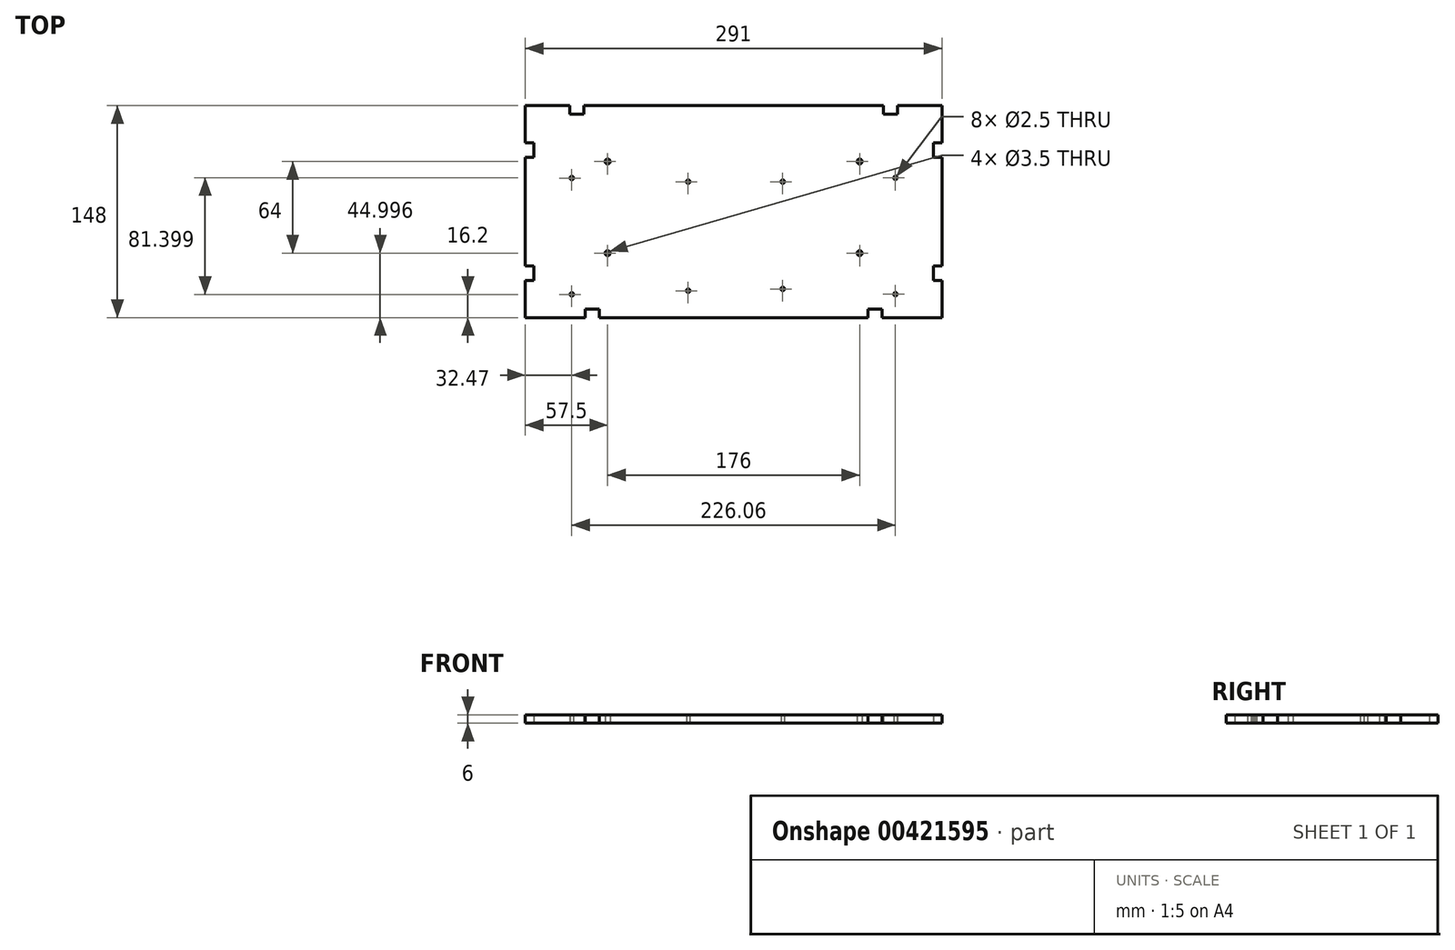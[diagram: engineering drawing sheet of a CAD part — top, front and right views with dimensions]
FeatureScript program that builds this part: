
annotation { "Feature Type Name" : "Feature", "Feature Type Description" : "" }
export const myFeature = defineFeature(function(context is Context, id is Id, definition is map)
    precondition{}
    {
        {
            var Q0;
            Q0=qCreatedBy(makeId("Top.planeOp"),FACE);
            var sketch = newSketch(context, id + "F0", { "sketchPlane" : qUnion([Q0])});
            skLineSegment(sketch, "E0", {"start": v(145.5, 47.8) * mm, "end": v(145.5, -28.2) * mm});
            skLineSegment(sketch, "E1", {"start": v(114.5, 83.8) * mm, "end": v(114.5, 77.8) * mm});
            skLineSegment(sketch, "E2", {"start": v(145.5, 83.8) * mm, "end": v(145.5, 57.8) * mm});
            skLineSegment(sketch, "E3", {"start": v(139.5, -38.2) * mm, "end": v(145.5, -38.2) * mm});
            skLineSegment(sketch, "E4", {"start": v(145.5, 57.8) * mm, "end": v(139.5, 57.8) * mm});
            skLineSegment(sketch, "E5", {"start": v(145.5, 47.8) * mm, "end": v(139.5, 47.8) * mm});
            skLineSegment(sketch, "E6", {"start": v(114.5, 83.8) * mm, "end": v(145.5, 83.8) * mm});
            skLineSegment(sketch, "E7", {"start": v(145.5, -38.2) * mm, "end": v(145.5, -64.2) * mm});
            skLineSegment(sketch, "E8", {"start": v(104.5, 83.8) * mm, "end": v(0, 83.8) * mm});
            skLineSegment(sketch, "E9.MirrorCS", {"start": v(-139.5, -38.2) * mm, "end": v(-145.5, -38.2) * mm});
            skLineSegment(sketch, "E10.MirrorCS", {"start": v(-114.5, 83.8) * mm, "end": v(-114.5, 77.8) * mm});
            skLineSegment(sketch, "E11.MirrorCS", {"start": v(-145.5, 83.8) * mm, "end": v(-145.5, 57.8) * mm});
            skLineSegment(sketch, "E12.MirrorCS", {"start": v(-145.5, -64.2) * mm, "end": v(-103.71, -64.2) * mm});
            skLineSegment(sketch, "E13.MirrorCS", {"start": v(-104.5, 83.8) * mm, "end": v(0, 83.8) * mm});
            skLineSegment(sketch, "E14.MirrorCS", {"start": v(-145.5, -38.2) * mm, "end": v(-145.5, -64.2) * mm});
            skLineSegment(sketch, "E15.MirrorCS", {"start": v(-93.67, -64.2) * mm, "end": v(0, -64.2) * mm});
            skLineSegment(sketch, "E16.MirrorCS", {"start": v(-114.5, 83.8) * mm, "end": v(-145.5, 83.8) * mm});
            skLineSegment(sketch, "E17.MirrorCS", {"start": v(-145.5, 47.8) * mm, "end": v(-145.5, -28.2) * mm});
            skCircle(sketch, "E18", {"center": v(-113.03, 33.28) * mm, "radius": 1.25 * mm});
            skCircle(sketch, "E19", {"center": v(-31.75, 30.74) * mm, "radius": 1.25 * mm});
            skCircle(sketch, "E20.MirrorC", {"center": v(113.03, 33.4) * mm, "radius": 1.25 * mm});
            skCircle(sketch, "E21.MirrorC", {"center": v(34.29, 30.74) * mm, "radius": 1.25 * mm});
            skCircle(sketch, "E22.MirrorC", {"center": v(113.03, -47.88) * mm, "radius": 1.25 * mm});
            skCircle(sketch, "E23.MirrorC", {"center": v(-31.75, -45.46) * mm, "radius": 1.25 * mm});
            skCircle(sketch, "E24.MirrorC", {"center": v(-113.03, -48) * mm, "radius": 1.25 * mm});
            skCircle(sketch, "E25", {"center": v(34.3, -44.2) * mm, "radius": 1.25 * mm});
            skLineSegment(sketch, "E26", {"start": v(103.71, -64.2) * mm, "end": v(145.5, -64.2) * mm});
            skLineSegment(sketch, "E27", {"start": v(0, -64.2) * mm, "end": v(93.67, -64.2) * mm});
            skCircle(sketch, "E28", {"center": v(-88, -19.2) * mm, "radius": 1.75 * mm});
            skCircle(sketch, "E29.MirrorC", {"center": v(88, -19.2) * mm, "radius": 1.75 * mm});
            skCircle(sketch, "E30", {"center": v(-88, 44.8) * mm, "radius": 1.75 * mm});
            skCircle(sketch, "E31.MirrorC", {"center": v(88, 44.8) * mm, "radius": 1.75 * mm});
            skLineSegment(sketch, "E32", {"start": v(114.5, 77.8) * mm, "end": v(104.5, 77.8) * mm});
            skLineSegment(sketch, "E33", {"start": v(104.5, 77.8) * mm, "end": v(104.5, 83.8) * mm});
            skLineSegment(sketch, "E34", {"start": v(139.5, 57.8) * mm, "end": v(139.5, 47.8) * mm});
            skLineSegment(sketch, "E35", {"start": v(139.5, -38.2) * mm, "end": v(139.5, -28.2) * mm});
            skLineSegment(sketch, "E36", {"start": v(139.5, -28.2) * mm, "end": v(145.5, -28.2) * mm});
            skLineSegment(sketch, "E37", {"start": v(103.71, -64.2) * mm, "end": v(103.71, -58.2) * mm});
            skLineSegment(sketch, "E38", {"start": v(103.71, -58.2) * mm, "end": v(93.67, -58.2) * mm});
            skLineSegment(sketch, "E39", {"start": v(93.67, -58.2) * mm, "end": v(93.67, -64.2) * mm});
            skLineSegment(sketch, "E40.MirrorCS", {"start": v(-103.71, -58.2) * mm, "end": v(-93.67, -58.2) * mm});
            skLineSegment(sketch, "E41.MirrorCS", {"start": v(-93.67, -58.2) * mm, "end": v(-93.67, -64.2) * mm});
            skLineSegment(sketch, "E42.MirrorCS", {"start": v(-103.71, -64.2) * mm, "end": v(-103.71, -58.2) * mm});
            skLineSegment(sketch, "E43.MirrorCS", {"start": v(-139.5, -38.2) * mm, "end": v(-139.5, -28.2) * mm});
            skLineSegment(sketch, "E44.MirrorCS", {"start": v(-139.5, -28.2) * mm, "end": v(-145.5, -28.2) * mm});
            skLineSegment(sketch, "E45.MirrorCS", {"start": v(-139.5, 57.8) * mm, "end": v(-139.5, 47.8) * mm});
            skLineSegment(sketch, "E46.MirrorCS", {"start": v(-145.5, 57.8) * mm, "end": v(-139.5, 57.8) * mm});
            skLineSegment(sketch, "E47.MirrorCS", {"start": v(-145.5, 47.8) * mm, "end": v(-139.5, 47.8) * mm});
            skLineSegment(sketch, "E48.MirrorCS", {"start": v(-114.5, 77.8) * mm, "end": v(-104.5, 77.8) * mm});
            skLineSegment(sketch, "E49.MirrorCS", {"start": v(-104.5, 77.8) * mm, "end": v(-104.5, 83.8) * mm});
            skSolve(sketch);
        }
        {
            var Q0;
            {var subQ2=sQuery(id+"F0.wireOp",EDGE,"XMeffzy6-l1vr-bFuy-l6tU-98MnWEfm23K2.bottom");Q0=makeQuery(id+"F0.imprint","IMPRINT",FACE,{"disambiguationData":[TD([[makeQuery(id+"F0.imprint","IMPRINT",EDGE,{"derivedFrom":subQ2}),1.0]])]});}
            var Q1;
            {var subQ0=sQuery(id+"F0.wireOp",EDGE,"LvRFwu82-oml2-OgSb-w6ea-0NJAzLZGbfFI");Q1=makeQuery(id+"F0.imprint","IMPRINT",FACE,{"disambiguationData":[TD([[makeQuery(id+"F0.imprint","IMPRINT",EDGE,{"derivedFrom":subQ0}),1.0]])]});}
            var Q2;
            {var subQ0=sQuery(id+"F0.wireOp",EDGE,"yimPrRvj-D9vO-SU7U-alxS-zAN60gq1FATs");Q2=makeQuery(id+"F0.imprint","IMPRINT",FACE,{"disambiguationData":[TD([[makeQuery(id+"F0.imprint","IMPRINT",EDGE,{"derivedFrom":subQ0}),1.0]])]});}
            var Q3;
            {var subQ0=sQuery(id+"F0.wireOp",EDGE,"LGuQCZRq-nD3X-KzUJ-cfye-xoDcGisW7mgL");Q3=makeQuery(id+"F0.imprint","IMPRINT",FACE,{"disambiguationData":[TD([[makeQuery(id+"F0.imprint","IMPRINT",EDGE,{"derivedFrom":subQ0}),1.0]])]});}
            var Q4;
            {var subQ0=sQuery(id+"F0.wireOp",EDGE,"TqfR0Gvf-FIE4-vlpR-C5RB-og33NBRcCtY9");Q4=makeQuery(id+"F0.imprint","IMPRINT",FACE,{"disambiguationData":[TD([[makeQuery(id+"F0.imprint","IMPRINT",EDGE,{"derivedFrom":subQ0}),1.0]])]});}
            var Q5;
            {var subQ2=sQuery(id+"F0.wireOp",EDGE,"vOMOrnyM-SsI4-R7wP-REIH-fPlN45hgWcFp.bottom");Q5=makeQuery(id+"F0.imprint","IMPRINT",FACE,{"disambiguationData":[TD([[makeQuery(id+"F0.imprint","IMPRINT",EDGE,{"derivedFrom":subQ2}),-1.0]])]});}
            var Q6;
            {var subQ2=sQuery(id+"F0.wireOp",EDGE,"DFXSyL9B-L4g9-x3Hx-7BQ8-nJkNfEQGhSC7.bottom");Q6=makeQuery(id+"F0.imprint","IMPRINT",FACE,{"disambiguationData":[TD([[makeQuery(id+"F0.imprint","IMPRINT",EDGE,{"derivedFrom":subQ2}),1.0]])]});}
            var Q7;
            {var subQ2=sQuery(id+"F0.wireOp",EDGE,"9RNaaaHk-bar6-hogj-ixjy-M610WzzZxztz.bottom");Q7=makeQuery(id+"F0.imprint","IMPRINT",FACE,{"disambiguationData":[TD([[makeQuery(id+"F0.imprint","IMPRINT",EDGE,{"derivedFrom":subQ2}),-1.0]])]});}
            var Q8;
            Q8=makeQuery(id+"F0.imprint","IMPRINT",FACE,{"disambiguationData":[TD([[makeQuery(id+"F0.imprint","IMPRINT",EDGE,{"derivedFrom":sQuery(id+"F0.wireOp",EDGE,"XMeffzy6-l1vr-bFuy-l6tU-98MnWEfm23K2.left")}),1.0]])]});
            var Q9;
            {var subQ4=sQuery(id+"F0.wireOp",EDGE,"d3399bb5-beab-43c9-a4a4-2bf1d94ea1638.MirrorCS");Q9=makeQuery(id+"F0.imprint","IMPRINT",FACE,{"disambiguationData":[TD([[makeQuery(id+"F0.imprint","IMPRINT",EDGE,{"derivedFrom":subQ4}),-1.0]])]});}
            var Q10;
            {var subQ0=sQuery(id+"F0.wireOp",EDGE,"d3399bb5-beab-43c9-a4a4-2bf1d94ea1634.MirrorCS");Q10=makeQuery(id+"F0.imprint","IMPRINT",FACE,{"disambiguationData":[TD([[makeQuery(id+"F0.imprint","IMPRINT",EDGE,{"derivedFrom":subQ0}),-1.0]])]});}
            var Q11;
            {var subQ0=sQuery(id+"F0.wireOp",EDGE,"44sCyGx3-ncb8-VNu2-eWKw-zJSuOeqNogZ8");Q11=makeQuery(id+"F0.imprint","IMPRINT",FACE,{"disambiguationData":[TD([[makeQuery(id+"F0.imprint","IMPRINT",EDGE,{"derivedFrom":subQ0}),1.0]])]});}
            var Q12;
            {var subQ0=sQuery(id+"F0.wireOp",EDGE,"9ca67261-c08b-4865-8187-171262c2a7f48.MirrorCS");Q12=makeQuery(id+"F0.imprint","IMPRINT",FACE,{"disambiguationData":[TD([[makeQuery(id+"F0.imprint","IMPRINT",EDGE,{"derivedFrom":subQ0}),-1.0]])]});}
            var Q13;
            {var subQ0=sQuery(id+"F0.wireOp",EDGE,"9ca67261-c08b-4865-8187-171262c2a7f411.MirrorCS");Q13=makeQuery(id+"F0.imprint","IMPRINT",FACE,{"disambiguationData":[TD([[makeQuery(id+"F0.imprint","IMPRINT",EDGE,{"derivedFrom":subQ0}),-1.0]])]});}
            var Q14;
            {var subQ4=sQuery(id+"F0.wireOp",EDGE,"275a21e3-fc4a-4418-a6b9-2f423d13b08316.MirrorCS");Q14=makeQuery(id+"F0.imprint","IMPRINT",FACE,{"disambiguationData":[TD([[makeQuery(id+"F0.imprint","IMPRINT",EDGE,{"derivedFrom":subQ4}),-1.0]])]});}
            var Q15;
            {var subQ4=sQuery(id+"F0.wireOp",EDGE,"275a21e3-fc4a-4418-a6b9-2f423d13b08312.MirrorCS");Q15=makeQuery(id+"F0.imprint","IMPRINT",FACE,{"disambiguationData":[TD([[makeQuery(id+"F0.imprint","IMPRINT",EDGE,{"derivedFrom":subQ4}),-1.0]])]});}
            var Q16;
            Q16=makeQuery(id+"F0.imprint","IMPRINT",FACE,{"disambiguationData":[TD([[makeQuery(id+"F0.imprint","IMPRINT",EDGE,{"derivedFrom":sQuery(id+"F0.wireOp",EDGE,"713078d0-e329-449e-9140-210a8ccc0fe10.MirrorCS")}),-1.0]])]});
            var Q17;
            Q17=makeQuery(id+"F0.imprint","IMPRINT",FACE,{"disambiguationData":[TD([[makeQuery(id+"F0.imprint","IMPRINT",EDGE,{"derivedFrom":sQuery(id+"F0.wireOp",EDGE,"E0")}),-1.0]])]});
            extrude(context, id + "F1", {"entities" : qUnion([Q0, Q1, Q2, Q3, Q4, Q5, Q6, Q7, Q8, Q9, Q10, Q11, Q12, Q13, Q14, Q15, Q16, Q17]), "depth" : 6 * mm, "offsetDistance" : 25 * mm});
        }
    });
